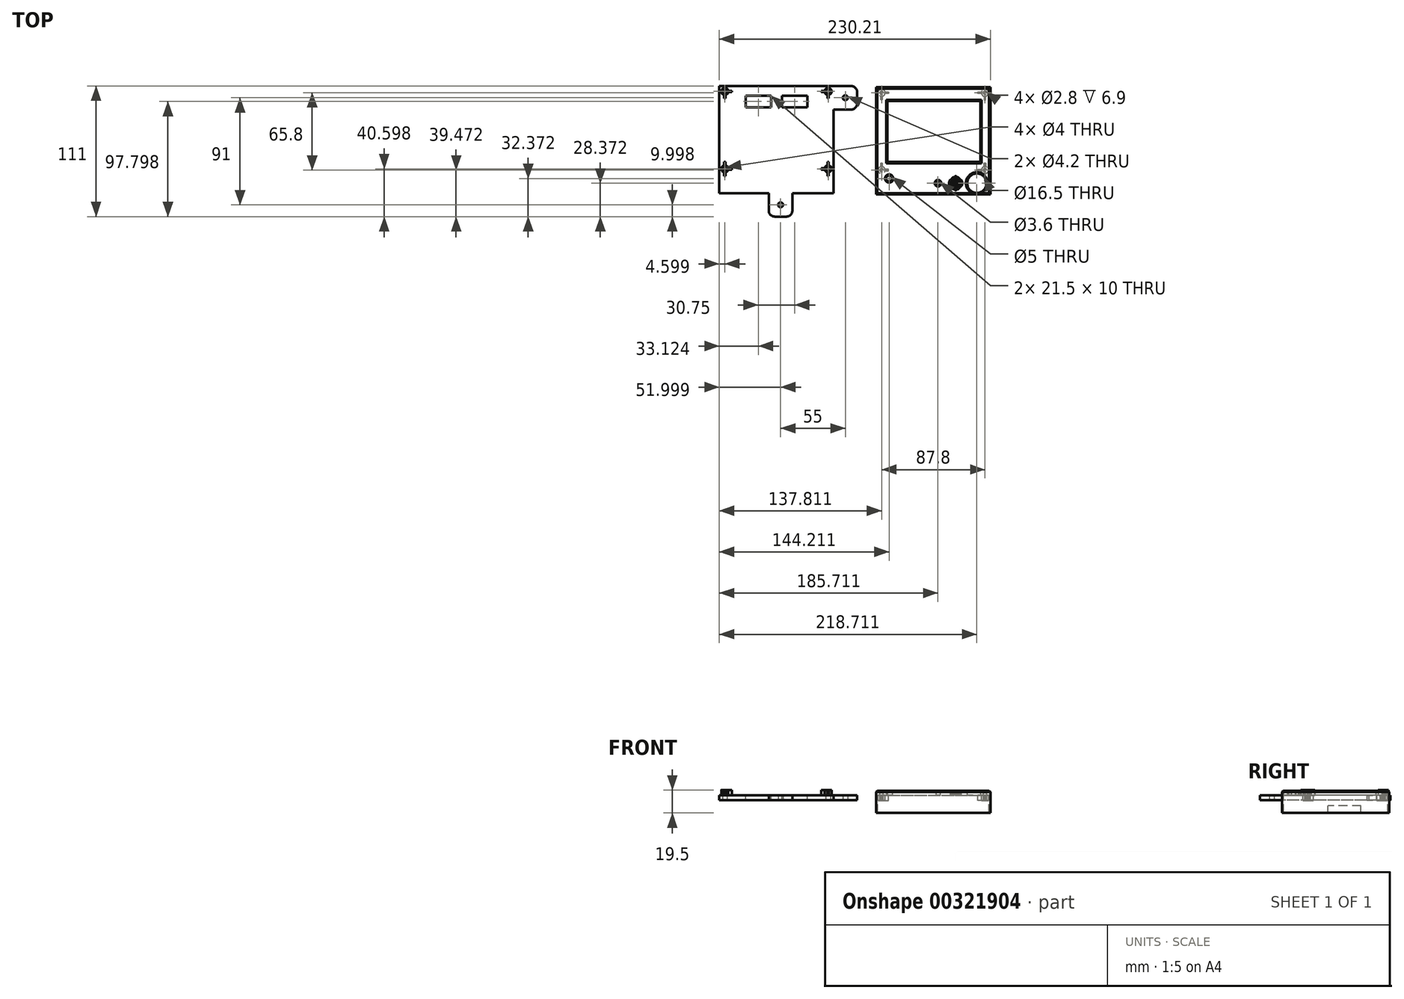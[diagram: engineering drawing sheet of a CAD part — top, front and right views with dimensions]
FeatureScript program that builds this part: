
annotation { "Feature Type Name" : "Feature", "Feature Type Description" : "" }
export const myFeature = defineFeature(function(context is Context, id is Id, definition is map)
    precondition{}
    {
        {
            var Q0;
            Q0=qCreatedBy(makeId("Top.planeOp"),FACE);
            var sketch = newSketch(context, id + "F0", { "sketchPlane" : qUnion([Q0])});
            skLineSegment(sketch, "E0.bottom", {"start": v(-33.99, 35.53) * mm, "end": v(63.01, 35.53) * mm});
            skLineSegment(sketch, "E0.top", {"start": v(-33.99, -55.47) * mm, "end": v(63.01, -55.47) * mm});
            skLineSegment(sketch, "E0.left", {"start": v(-33.99, 35.53) * mm, "end": v(-33.99, -55.47) * mm});
            skLineSegment(sketch, "E0.right", {"start": v(63.01, 35.53) * mm, "end": v(63.01, -55.47) * mm});
            skLineSegment(sketch, "E1.bottom", {"start": v(-24.49, 24.03) * mm, "end": v(54.51, 24.03) * mm});
            skLineSegment(sketch, "E1.top", {"start": v(-24.49, -27.97) * mm, "end": v(54.51, -27.97) * mm});
            skLineSegment(sketch, "E1.left", {"start": v(-24.49, 24.03) * mm, "end": v(-24.49, -27.97) * mm});
            skLineSegment(sketch, "E1.right", {"start": v(54.51, 24.03) * mm, "end": v(54.51, -27.97) * mm});
            skCircle(sketch, "E2", {"center": v(-29.39, 30.93) * mm, "radius": 1.4 * mm});
            skCircle(sketch, "E3", {"center": v(58.41, 30.93) * mm, "radius": 1.4 * mm});
            skCircle(sketch, "E4", {"center": v(58.41, -34.87) * mm, "radius": 1.4 * mm});
            skCircle(sketch, "E5", {"center": v(-29.39, -34.87) * mm, "radius": 1.4 * mm});
            skCircle(sketch, "E6", {"center": v(51.51, -45.97) * mm, "radius": 8.25 * mm});
            skEllipse(sketch, "E7", {"center": v(33.51, -45.97) * mm, "majorRadius": 5 * mm, "minorRadius": 0.55 * mm, "majorAxis": v(0, -1)});
            skEllipse(sketch, "E8", {"center": v(31.51, -45.97) * mm, "majorRadius": 4 * mm, "minorRadius": 0.55 * mm, "majorAxis": v(0, -1)});
            skEllipse(sketch, "E9", {"center": v(29.51, -45.97) * mm, "majorRadius": 2 * mm, "minorRadius": 0.55 * mm, "majorAxis": v(0, -1)});
            skEllipse(sketch, "E10", {"center": v(35.51, -45.97) * mm, "majorRadius": 4 * mm, "minorRadius": 0.55 * mm, "majorAxis": v(0, -1)});
            skPoint(sketch, "E10.centerSnap0", {"position": v(34.06, -45.97) * mm});
            skEllipse(sketch, "E11", {"center": v(37.51, -45.97) * mm, "majorRadius": 2 * mm, "minorRadius": 0.55 * mm, "majorAxis": v(0, -1)});
            skCircle(sketch, "E12", {"center": v(18.51, -45.97) * mm, "radius": 1.8 * mm});
            skPoint(sketch, "E12.centerSnap0", {"position": v(32.96, -45.97) * mm});
            skCircle(sketch, "E13", {"center": v(-22.99, -41.97) * mm, "radius": 2.5 * mm});
            skSolve(sketch);
        }
        {
            var Q0;
            Q0=makeQuery(id+"F0.imprint","IMPRINT",FACE,{"disambiguationData":[TD([[makeQuery(id+"F0.imprint","IMPRINT",EDGE,{"derivedFrom":sQuery(id+"F0.wireOp",EDGE,"E0.bottom")}),-1.0]])]});
            var Q1;
            Q1=makeQuery(id+"F0.imprint","IMPRINT",FACE,{"disambiguationData":[TD([[makeQuery(id+"F0.imprint","IMPRINT",EDGE,{"derivedFrom":sQuery(id+"F0.wireOp",EDGE,"E2")}),1.0]])]});
            var Q2;
            Q2=makeQuery(id+"F0.imprint","IMPRINT",FACE,{"disambiguationData":[TD([[makeQuery(id+"F0.imprint","IMPRINT",EDGE,{"derivedFrom":sQuery(id+"F0.wireOp",EDGE,"E5")}),1.0]])]});
            var Q3;
            Q3=makeQuery(id+"F0.imprint","IMPRINT",FACE,{"disambiguationData":[TD([[makeQuery(id+"F0.imprint","IMPRINT",EDGE,{"derivedFrom":sQuery(id+"F0.wireOp",EDGE,"E4")}),1.0]])]});
            var Q4;
            Q4=makeQuery(id+"F0.imprint","IMPRINT",FACE,{"disambiguationData":[TD([[makeQuery(id+"F0.imprint","IMPRINT",EDGE,{"derivedFrom":sQuery(id+"F0.wireOp",EDGE,"E3")}),1.0]])]});
            extrude(context, id + "F1", {"entities" : qUnion([Q0, Q1, Q2, Q3, Q4]), "depth" : 4 * mm});
        }
        {
            var Q0;
            Q0=makeQuery(id+"F1.opExtrude","CAP_FACE",FACE,{"disambiguationData":[OSD([sQuery(id+"F0.wireOp",EDGE,"E0.bottom"),sQuery(id+"F0.wireOp",EDGE,"E0.top"),sQuery(id+"F0.wireOp",EDGE,"E0.left"),sQuery(id+"F0.wireOp",EDGE,"E0.right"),sQuery(id+"F0.wireOp",EDGE,"E1.bottom"),sQuery(id+"F0.wireOp",EDGE,"E1.top"),sQuery(id+"F0.wireOp",EDGE,"E1.left"),sQuery(id+"F0.wireOp",EDGE,"E1.right"),sQuery(id+"F0.wireOp",EDGE,"E2"),sQuery(id+"F0.wireOp",EDGE,"E3"),sQuery(id+"F0.wireOp",EDGE,"E4"),sQuery(id+"F0.wireOp",EDGE,"E5"),sQuery(id+"F0.wireOp",EDGE,"E6"),sQuery(id+"F0.wireOp",EDGE,"E7"),sQuery(id+"F0.wireOp",EDGE,"E8"),sQuery(id+"F0.wireOp",EDGE,"E9"),sQuery(id+"F0.wireOp",EDGE,"E10"),sQuery(id+"F0.wireOp",EDGE,"E11"),sQuery(id+"F0.wireOp",EDGE,"E12"),sQuery(id+"F0.wireOp",EDGE,"E13")])],"isStart":true});
            var sketch = newSketch(context, id + "F2", { "sketchPlane" : qUnion([Q0])});
            skCircle(sketch, "E14", {"center": v(58.41, -30.93) * mm, "radius": 1.4 * mm});
            skCircle(sketch, "E15", {"center": v(-29.39, -30.93) * mm, "radius": 1.4 * mm});
            skCircle(sketch, "E16", {"center": v(-29.39, 34.87) * mm, "radius": 1.4 * mm});
            skCircle(sketch, "E17", {"center": v(58.41, 34.87) * mm, "radius": 1.4 * mm});
            skLineSegment(sketch, "E18", {"start": v(61.81, -34.33) * mm, "end": v(-32.79, -34.33) * mm});
            skLineSegment(sketch, "E19", {"start": v(-32.79, -34.33) * mm, "end": v(-32.79, 54.27) * mm});
            skLineSegment(sketch, "E20", {"start": v(-32.79, 54.27) * mm, "end": v(61.81, 54.27) * mm});
            skLineSegment(sketch, "E21", {"start": v(61.81, 54.27) * mm, "end": v(61.81, -34.33) * mm});
            skCircle(sketch, "E22", {"center": v(58.41, -30.93) * mm, "radius": 3 * mm});
            skCircle(sketch, "E23", {"center": v(58.41, 34.87) * mm, "radius": 3 * mm});
            skCircle(sketch, "E24", {"center": v(-29.39, 34.87) * mm, "radius": 3 * mm});
            skCircle(sketch, "E25", {"center": v(-29.39, -30.93) * mm, "radius": 3 * mm});
            skLineSegment(sketch, "E26", {"start": v(55.47, 35.47) * mm, "end": v(52.41, 35.47) * mm});
            skLineSegment(sketch, "E27", {"start": v(52.41, 35.47) * mm, "end": v(52.41, 34.27) * mm});
            skLineSegment(sketch, "E28", {"start": v(52.41, 34.27) * mm, "end": v(55.47, 34.27) * mm});
            skLineSegment(sketch, "E29", {"start": v(57.81, 31.93) * mm, "end": v(57.81, 28.87) * mm});
            skLineSegment(sketch, "E30", {"start": v(57.81, 28.87) * mm, "end": v(59.01, 28.87) * mm});
            skLineSegment(sketch, "E31", {"start": v(59.01, 28.87) * mm, "end": v(59.01, 31.93) * mm});
            skLineSegment(sketch, "E32", {"start": v(57.81, -28) * mm, "end": v(57.81, -24.93) * mm});
            skLineSegment(sketch, "E33", {"start": v(57.81, -24.93) * mm, "end": v(59.01, -24.93) * mm});
            skLineSegment(sketch, "E34", {"start": v(59.01, -24.93) * mm, "end": v(59.01, -28) * mm});
            skLineSegment(sketch, "E35", {"start": v(55.47, -30.33) * mm, "end": v(52.41, -30.33) * mm});
            skLineSegment(sketch, "E36", {"start": v(52.41, -30.33) * mm, "end": v(52.41, -31.53) * mm});
            skLineSegment(sketch, "E37", {"start": v(52.41, -31.53) * mm, "end": v(55.47, -31.53) * mm});
            skLineSegment(sketch, "E38", {"start": v(-26.45, -31.53) * mm, "end": v(-23.39, -31.53) * mm});
            skLineSegment(sketch, "E39", {"start": v(-23.39, -31.53) * mm, "end": v(-23.39, -30.33) * mm});
            skLineSegment(sketch, "E40", {"start": v(-23.39, -30.33) * mm, "end": v(-26.45, -30.33) * mm});
            skLineSegment(sketch, "E41", {"start": v(-28.79, -28) * mm, "end": v(-28.79, -24.93) * mm});
            skLineSegment(sketch, "E42", {"start": v(-28.79, -24.93) * mm, "end": v(-29.99, -24.93) * mm});
            skLineSegment(sketch, "E43", {"start": v(-29.99, -24.93) * mm, "end": v(-29.99, -28) * mm});
            skLineSegment(sketch, "E44", {"start": v(-29.99, 31.93) * mm, "end": v(-29.99, 28.87) * mm});
            skLineSegment(sketch, "E45", {"start": v(-29.99, 28.87) * mm, "end": v(-28.79, 28.87) * mm});
            skLineSegment(sketch, "E46", {"start": v(-28.79, 28.87) * mm, "end": v(-28.79, 31.93) * mm});
            skLineSegment(sketch, "E47", {"start": v(-26.45, 35.47) * mm, "end": v(-23.39, 35.47) * mm});
            skLineSegment(sketch, "E48", {"start": v(-23.39, 35.47) * mm, "end": v(-23.39, 34.27) * mm});
            skLineSegment(sketch, "E49", {"start": v(-23.39, 34.27) * mm, "end": v(-26.45, 34.27) * mm});
            skSolve(sketch);
        }
        {
            var Q0;
            Q0=makeQuery(id+"F2.imprint","IMPRINT",FACE,{"disambiguationData":[TD([[makeQuery(id+"F2.imprint","IMPRINT",EDGE,{"derivedFrom":sQuery(id+"F2.wireOp",EDGE,"E18")}),1.0]])]});
            extrude(context, id + "F3", {"entities" : qUnion([Q0]), "operationType" : NewBodyOperationType.ADD, "depth" : 15 * mm});
        }
        {
            var Q0;
            Q0=makeQuery(id+"F2.imprint","IMPRINT",FACE,{"disambiguationData":[TD([[makeQuery(id+"F2.imprint","IMPRINT",EDGE,{"derivedFrom":sQuery(id+"F2.wireOp",EDGE,"E14")}),-1.0]])]});
            var Q1;
            Q1=makeQuery(id+"F2.imprint","IMPRINT",FACE,{"disambiguationData":[TD([[makeQuery(id+"F2.imprint","IMPRINT",EDGE,{"derivedFrom":sQuery(id+"F2.wireOp",EDGE,"E17")}),-1.0]])]});
            var Q2;
            Q2=makeQuery(id+"F2.imprint","IMPRINT",FACE,{"disambiguationData":[TD([[makeQuery(id+"F2.imprint","IMPRINT",EDGE,{"derivedFrom":sQuery(id+"F2.wireOp",EDGE,"E15")}),-1.0]])]});
            var Q3;
            Q3=makeQuery(id+"F2.imprint","IMPRINT",FACE,{"disambiguationData":[TD([[makeQuery(id+"F2.imprint","IMPRINT",EDGE,{"derivedFrom":sQuery(id+"F2.wireOp",EDGE,"E16")}),-1.0]])]});
            var Q4;
            {var subQ0=sQuery(id+"F2.wireOp",EDGE,"E44");Q4=makeQuery(id+"F2.imprint","IMPRINT",FACE,{"disambiguationData":[TD([[makeQuery(id+"F2.imprint","IMPRINT",EDGE,{"derivedFrom":subQ0}),1.0]])]});}
            var Q5;
            {var subQ0=sQuery(id+"F2.wireOp",EDGE,"E47");Q5=makeQuery(id+"F2.imprint","IMPRINT",FACE,{"disambiguationData":[TD([[makeQuery(id+"F2.imprint","IMPRINT",EDGE,{"derivedFrom":subQ0}),-1.0]])]});}
            var Q6;
            {var subQ0=sQuery(id+"F2.wireOp",EDGE,"E41");Q6=makeQuery(id+"F2.imprint","IMPRINT",FACE,{"disambiguationData":[TD([[makeQuery(id+"F2.imprint","IMPRINT",EDGE,{"derivedFrom":subQ0}),1.0]])]});}
            var Q7;
            {var subQ0=sQuery(id+"F2.wireOp",EDGE,"E38");Q7=makeQuery(id+"F2.imprint","IMPRINT",FACE,{"disambiguationData":[TD([[makeQuery(id+"F2.imprint","IMPRINT",EDGE,{"derivedFrom":subQ0}),1.0]])]});}
            var Q8;
            {var subQ0=sQuery(id+"F2.wireOp",EDGE,"E26");Q8=makeQuery(id+"F2.imprint","IMPRINT",FACE,{"disambiguationData":[TD([[makeQuery(id+"F2.imprint","IMPRINT",EDGE,{"derivedFrom":subQ0}),1.0]])]});}
            var Q9;
            {var subQ0=sQuery(id+"F2.wireOp",EDGE,"E29");Q9=makeQuery(id+"F2.imprint","IMPRINT",FACE,{"disambiguationData":[TD([[makeQuery(id+"F2.imprint","IMPRINT",EDGE,{"derivedFrom":subQ0}),1.0]])]});}
            var Q10;
            {var subQ0=sQuery(id+"F2.wireOp",EDGE,"E32");Q10=makeQuery(id+"F2.imprint","IMPRINT",FACE,{"disambiguationData":[TD([[makeQuery(id+"F2.imprint","IMPRINT",EDGE,{"derivedFrom":subQ0}),-1.0]])]});}
            var Q11;
            {var subQ0=sQuery(id+"F2.wireOp",EDGE,"E35");Q11=makeQuery(id+"F2.imprint","IMPRINT",FACE,{"disambiguationData":[TD([[makeQuery(id+"F2.imprint","IMPRINT",EDGE,{"derivedFrom":subQ0}),1.0]])]});}
            extrude(context, id + "F4", {"entities" : qUnion([Q0, Q1, Q2, Q3, Q4, Q5, Q6, Q7, Q8, Q9, Q10, Q11]), "operationType" : NewBodyOperationType.ADD, "depth" : 4.5 * mm});
        }
        {
            var Q0;
            Q0=makeQuery(id+"F4.boolean.opBoolean","SPLIT",FACE,{"disambiguationData":[TD([makeQuery(id+"F4.opExtrude","SWEPT_FACE",FACE,{"disambiguationData":[OSD([sQuery(id+"F2.wireOp",EDGE,"E15")])]})])],"derivedFrom":makeQuery(id+"F1.opExtrude","CAP_FACE",FACE,{"disambiguationData":[OSD([sQuery(id+"F0.wireOp",EDGE,"E0.bottom"),sQuery(id+"F0.wireOp",EDGE,"E0.top"),sQuery(id+"F0.wireOp",EDGE,"E0.left"),sQuery(id+"F0.wireOp",EDGE,"E0.right"),sQuery(id+"F0.wireOp",EDGE,"E1.bottom"),sQuery(id+"F0.wireOp",EDGE,"E1.top"),sQuery(id+"F0.wireOp",EDGE,"E1.left"),sQuery(id+"F0.wireOp",EDGE,"E1.right"),sQuery(id+"F0.wireOp",EDGE,"E6"),sQuery(id+"F0.wireOp",EDGE,"E7"),sQuery(id+"F0.wireOp",EDGE,"E8"),sQuery(id+"F0.wireOp",EDGE,"E9"),sQuery(id+"F0.wireOp",EDGE,"E10"),sQuery(id+"F0.wireOp",EDGE,"E11"),sQuery(id+"F0.wireOp",EDGE,"E12"),sQuery(id+"F0.wireOp",EDGE,"E13")])],"isStart":true})});
            var Q1;
            Q1=makeQuery(id+"F4.boolean.opBoolean","SPLIT",FACE,{"disambiguationData":[TD([makeQuery(id+"F4.opExtrude","SWEPT_FACE",FACE,{"disambiguationData":[OSD([sQuery(id+"F2.wireOp",EDGE,"E16")])]})])],"derivedFrom":makeQuery(id+"F1.opExtrude","CAP_FACE",FACE,{"disambiguationData":[OSD([sQuery(id+"F0.wireOp",EDGE,"E0.bottom"),sQuery(id+"F0.wireOp",EDGE,"E0.top"),sQuery(id+"F0.wireOp",EDGE,"E0.left"),sQuery(id+"F0.wireOp",EDGE,"E0.right"),sQuery(id+"F0.wireOp",EDGE,"E1.bottom"),sQuery(id+"F0.wireOp",EDGE,"E1.top"),sQuery(id+"F0.wireOp",EDGE,"E1.left"),sQuery(id+"F0.wireOp",EDGE,"E1.right"),sQuery(id+"F0.wireOp",EDGE,"E6"),sQuery(id+"F0.wireOp",EDGE,"E7"),sQuery(id+"F0.wireOp",EDGE,"E8"),sQuery(id+"F0.wireOp",EDGE,"E9"),sQuery(id+"F0.wireOp",EDGE,"E10"),sQuery(id+"F0.wireOp",EDGE,"E11"),sQuery(id+"F0.wireOp",EDGE,"E12"),sQuery(id+"F0.wireOp",EDGE,"E13")])],"isStart":true})});
            var Q2;
            Q2=makeQuery(id+"F4.boolean.opBoolean","SPLIT",FACE,{"disambiguationData":[TD([makeQuery(id+"F4.opExtrude","SWEPT_FACE",FACE,{"disambiguationData":[OSD([sQuery(id+"F2.wireOp",EDGE,"E17")])]})])],"derivedFrom":makeQuery(id+"F1.opExtrude","CAP_FACE",FACE,{"disambiguationData":[OSD([sQuery(id+"F0.wireOp",EDGE,"E0.bottom"),sQuery(id+"F0.wireOp",EDGE,"E0.top"),sQuery(id+"F0.wireOp",EDGE,"E0.left"),sQuery(id+"F0.wireOp",EDGE,"E0.right"),sQuery(id+"F0.wireOp",EDGE,"E1.bottom"),sQuery(id+"F0.wireOp",EDGE,"E1.top"),sQuery(id+"F0.wireOp",EDGE,"E1.left"),sQuery(id+"F0.wireOp",EDGE,"E1.right"),sQuery(id+"F0.wireOp",EDGE,"E6"),sQuery(id+"F0.wireOp",EDGE,"E7"),sQuery(id+"F0.wireOp",EDGE,"E8"),sQuery(id+"F0.wireOp",EDGE,"E9"),sQuery(id+"F0.wireOp",EDGE,"E10"),sQuery(id+"F0.wireOp",EDGE,"E11"),sQuery(id+"F0.wireOp",EDGE,"E12"),sQuery(id+"F0.wireOp",EDGE,"E13")])],"isStart":true})});
            var Q3;
            Q3=makeQuery(id+"F4.boolean.opBoolean","SPLIT",FACE,{"disambiguationData":[TD([makeQuery(id+"F4.opExtrude","SWEPT_FACE",FACE,{"disambiguationData":[OSD([sQuery(id+"F2.wireOp",EDGE,"E14")])]})])],"derivedFrom":makeQuery(id+"F1.opExtrude","CAP_FACE",FACE,{"disambiguationData":[OSD([sQuery(id+"F0.wireOp",EDGE,"E0.bottom"),sQuery(id+"F0.wireOp",EDGE,"E0.top"),sQuery(id+"F0.wireOp",EDGE,"E0.left"),sQuery(id+"F0.wireOp",EDGE,"E0.right"),sQuery(id+"F0.wireOp",EDGE,"E1.bottom"),sQuery(id+"F0.wireOp",EDGE,"E1.top"),sQuery(id+"F0.wireOp",EDGE,"E1.left"),sQuery(id+"F0.wireOp",EDGE,"E1.right"),sQuery(id+"F0.wireOp",EDGE,"E6"),sQuery(id+"F0.wireOp",EDGE,"E7"),sQuery(id+"F0.wireOp",EDGE,"E8"),sQuery(id+"F0.wireOp",EDGE,"E9"),sQuery(id+"F0.wireOp",EDGE,"E10"),sQuery(id+"F0.wireOp",EDGE,"E11"),sQuery(id+"F0.wireOp",EDGE,"E12"),sQuery(id+"F0.wireOp",EDGE,"E13")])],"isStart":true})});
            extrude(context, id + "F5", {"entities" : qUnion([Q0, Q1, Q2, Q3]), "operationType" : NewBodyOperationType.REMOVE, "oppositeDirection" : true, "depth" : 2.4 * mm});
        }
        {
            var Q0;
            {var subQ0=sQuery(id+"F0.wireOp",EDGE,"E0.left");Q0=makeQuery(id+"F3.boolean.opBoolean","MERGE",FACE,{"derivedFrom":[makeQuery(id+"F1.opExtrude","SWEPT_FACE",FACE,{"disambiguationData":[OSD([subQ0])]}),makeQuery(id+"F3.opExtrude","SWEPT_FACE",FACE,{"disambiguationData":[OSD([subQ0])]})]});}
            var sketch = newSketch(context, id + "F6", { "sketchPlane" : qUnion([Q0])});
            skLineSegment(sketch, "E50.bottom", {"start": v(-11.53, -15) * mm, "end": v(16.47, -15) * mm});
            skLineSegment(sketch, "E50.top", {"start": v(-11.53, -9) * mm, "end": v(16.47, -9) * mm});
            skLineSegment(sketch, "E50.left", {"start": v(-11.53, -15) * mm, "end": v(-11.53, -9) * mm});
            skLineSegment(sketch, "E50.right", {"start": v(16.47, -15) * mm, "end": v(16.47, -9) * mm});
            skSolve(sketch);
        }
        {
            var Q0;
            Q0=makeQuery(id+"F6.imprint","IMPRINT",FACE,{"disambiguationData":[TD([[makeQuery(id+"F6.imprint","IMPRINT",EDGE,{"derivedFrom":sQuery(id+"F6.wireOp",EDGE,"E50.bottom")}),1.0]])]});
            extrude(context, id + "F7", {"entities" : qUnion([Q0]), "operationType" : NewBodyOperationType.REMOVE, "oppositeDirection" : true, "depth" : 2 * mm});
        }
        {
            var Q0;
            Q0=makeQuery(id+"F1.opExtrude","CAP_FACE",FACE,{"disambiguationData":[OSD([sQuery(id+"F0.wireOp",EDGE,"E0.bottom"),sQuery(id+"F0.wireOp",EDGE,"E0.top"),sQuery(id+"F0.wireOp",EDGE,"E0.left"),sQuery(id+"F0.wireOp",EDGE,"E0.right"),sQuery(id+"F0.wireOp",EDGE,"E1.bottom"),sQuery(id+"F0.wireOp",EDGE,"E1.top"),sQuery(id+"F0.wireOp",EDGE,"E1.left"),sQuery(id+"F0.wireOp",EDGE,"E1.right"),sQuery(id+"F0.wireOp",EDGE,"E6"),sQuery(id+"F0.wireOp",EDGE,"E7"),sQuery(id+"F0.wireOp",EDGE,"E8"),sQuery(id+"F0.wireOp",EDGE,"E9"),sQuery(id+"F0.wireOp",EDGE,"E10"),sQuery(id+"F0.wireOp",EDGE,"E11"),sQuery(id+"F0.wireOp",EDGE,"E12"),sQuery(id+"F0.wireOp",EDGE,"E13")])],"isStart":false});
            chamfer(context, id + "F8", {"entities" : qUnion([Q0]), "width" : 1 * mm, "tangentPropagation" : true});
        }
        {
            var Q0;
            Q0=qCreatedBy(makeId("Top.planeOp"),FACE);
            var sketch = newSketch(context, id + "F9", { "sketchPlane" : qUnion([Q0])});
            skLineSegment(sketch, "E51.bottom", {"start": v(-167.2, 36.66) * mm, "end": v(-70.2, 36.66) * mm});
            skLineSegment(sketch, "E51.top", {"start": v(-167.2, -54.34) * mm, "end": v(-70.2, -54.34) * mm});
            skLineSegment(sketch, "E51.left", {"start": v(-167.2, 36.66) * mm, "end": v(-167.2, -54.34) * mm});
            skLineSegment(sketch, "E51.right", {"start": v(-70.2, 36.66) * mm, "end": v(-70.2, -54.34) * mm});
            skLineSegment(sketch, "E52.bottom", {"start": v(-166, 35.46) * mm, "end": v(-71.4, 35.46) * mm});
            skLineSegment(sketch, "E52.top", {"start": v(-166, -53.14) * mm, "end": v(-71.4, -53.14) * mm});
            skLineSegment(sketch, "E52.left", {"start": v(-166, 35.46) * mm, "end": v(-166, -53.14) * mm});
            skLineSegment(sketch, "E52.right", {"start": v(-71.4, 35.46) * mm, "end": v(-71.4, -53.14) * mm});
            skCircle(sketch, "E53", {"center": v(-162.6, 32.06) * mm, "radius": 2 * mm});
            skCircle(sketch, "E54", {"center": v(-74.8, 32.06) * mm, "radius": 2 * mm});
            skCircle(sketch, "E55", {"center": v(-162.6, -33.74) * mm, "radius": 2 * mm});
            skCircle(sketch, "E56", {"center": v(-74.8, -33.74) * mm, "radius": 2 * mm});
            skLineSegment(sketch, "E57", {"start": v(-71.4, -33.74) * mm, "end": v(-71.4, -33.74) * mm});
            skLineSegment(sketch, "E58.bottom", {"start": v(-144.83, 28.46) * mm, "end": v(-123.33, 28.46) * mm});
            skLineSegment(sketch, "E58.top", {"start": v(-144.83, 18.46) * mm, "end": v(-123.33, 18.46) * mm});
            skLineSegment(sketch, "E58.left", {"start": v(-144.83, 28.46) * mm, "end": v(-144.83, 18.46) * mm});
            skLineSegment(sketch, "E58.right", {"start": v(-123.33, 28.46) * mm, "end": v(-123.33, 18.46) * mm});
            skLineSegment(sketch, "E59.bottom", {"start": v(-114.08, 28.46) * mm, "end": v(-92.58, 28.46) * mm});
            skLineSegment(sketch, "E59.top", {"start": v(-114.08, 18.46) * mm, "end": v(-92.58, 18.46) * mm});
            skLineSegment(sketch, "E59.left", {"start": v(-114.08, 28.46) * mm, "end": v(-114.08, 18.46) * mm});
            skLineSegment(sketch, "E59.right", {"start": v(-92.58, 28.46) * mm, "end": v(-92.58, 18.46) * mm});
            skCircle(sketch, "E60", {"center": v(-74.8, 32.06) * mm, "radius": 3 * mm});
            skCircle(sketch, "E61", {"center": v(-162.6, 32.06) * mm, "radius": 3 * mm});
            skCircle(sketch, "E62", {"center": v(-74.8, -33.74) * mm, "radius": 3 * mm});
            skCircle(sketch, "E63", {"center": v(-162.6, -33.74) * mm, "radius": 3 * mm});
            skLineSegment(sketch, "E64", {"start": v(-163.2, 29.12) * mm, "end": v(-163.2, 26.06) * mm});
            skLineSegment(sketch, "E65", {"start": v(-163.2, 26.06) * mm, "end": v(-162, 26.06) * mm});
            skLineSegment(sketch, "E66", {"start": v(-162, 26.06) * mm, "end": v(-162, 29.12) * mm});
            skLineSegment(sketch, "E67", {"start": v(-159.66, 32.66) * mm, "end": v(-156.6, 32.66) * mm});
            skLineSegment(sketch, "E68", {"start": v(-156.6, 32.66) * mm, "end": v(-156.6, 31.46) * mm});
            skLineSegment(sketch, "E69", {"start": v(-156.6, 31.46) * mm, "end": v(-159.66, 31.46) * mm});
            skLineSegment(sketch, "E70", {"start": v(-163.2, -30.8) * mm, "end": v(-163.2, -27.74) * mm});
            skLineSegment(sketch, "E71", {"start": v(-163.2, -27.74) * mm, "end": v(-162, -27.74) * mm});
            skLineSegment(sketch, "E72", {"start": v(-162, -27.74) * mm, "end": v(-162, -30.8) * mm});
            skLineSegment(sketch, "E73", {"start": v(-159.66, -33.14) * mm, "end": v(-156.6, -33.14) * mm});
            skLineSegment(sketch, "E74", {"start": v(-156.6, -33.14) * mm, "end": v(-156.6, -34.34) * mm});
            skLineSegment(sketch, "E75", {"start": v(-156.6, -34.34) * mm, "end": v(-159.66, -34.34) * mm});
            skLineSegment(sketch, "E76", {"start": v(-162, -36.68) * mm, "end": v(-162, -39.74) * mm});
            skLineSegment(sketch, "E77", {"start": v(-162, -39.74) * mm, "end": v(-163.2, -39.74) * mm});
            skLineSegment(sketch, "E78", {"start": v(-163.2, -39.74) * mm, "end": v(-163.2, -36.68) * mm});
            skLineSegment(sketch, "E79", {"start": v(-75.4, -30.8) * mm, "end": v(-75.4, -27.74) * mm});
            skLineSegment(sketch, "E80", {"start": v(-75.4, -27.74) * mm, "end": v(-74.2, -27.74) * mm});
            skLineSegment(sketch, "E81", {"start": v(-74.2, -27.74) * mm, "end": v(-74.2, -30.8) * mm});
            skLineSegment(sketch, "E82", {"start": v(-77.74, -33.14) * mm, "end": v(-80.8, -33.14) * mm});
            skLineSegment(sketch, "E83", {"start": v(-80.8, -33.14) * mm, "end": v(-80.8, -34.34) * mm});
            skLineSegment(sketch, "E84", {"start": v(-80.8, -34.34) * mm, "end": v(-77.74, -34.34) * mm});
            skLineSegment(sketch, "E85", {"start": v(-75.4, -36.68) * mm, "end": v(-75.4, -39.74) * mm});
            skLineSegment(sketch, "E86", {"start": v(-75.4, -39.74) * mm, "end": v(-74.2, -39.74) * mm});
            skLineSegment(sketch, "E87", {"start": v(-74.2, -39.74) * mm, "end": v(-74.2, -36.68) * mm});
            skLineSegment(sketch, "E88", {"start": v(-77.74, 32.66) * mm, "end": v(-80.8, 32.66) * mm});
            skLineSegment(sketch, "E89", {"start": v(-80.8, 32.66) * mm, "end": v(-80.8, 31.46) * mm});
            skLineSegment(sketch, "E90", {"start": v(-80.8, 31.46) * mm, "end": v(-77.74, 31.46) * mm});
            skLineSegment(sketch, "E91", {"start": v(-75.4, 29.12) * mm, "end": v(-75.4, 26.06) * mm});
            skLineSegment(sketch, "E92", {"start": v(-75.4, 26.06) * mm, "end": v(-74.2, 26.06) * mm});
            skLineSegment(sketch, "E93", {"start": v(-74.2, 26.06) * mm, "end": v(-74.2, 29.12) * mm});
            skSolve(sketch);
        }
        {
            var Q0;
            Q0=makeQuery(id+"F9.imprint","IMPRINT",FACE,{"disambiguationData":[TD([[makeQuery(id+"F9.imprint","IMPRINT",EDGE,{"derivedFrom":sQuery(id+"F9.wireOp",EDGE,"E53")}),-1.0]])]});
            var Q1;
            Q1=makeQuery(id+"F9.imprint","IMPRINT",FACE,{"disambiguationData":[TD([[makeQuery(id+"F9.imprint","IMPRINT",EDGE,{"derivedFrom":sQuery(id+"F9.wireOp",EDGE,"E54")}),-1.0]])]});
            var Q2;
            Q2=makeQuery(id+"F9.imprint","IMPRINT",FACE,{"disambiguationData":[TD([[makeQuery(id+"F9.imprint","IMPRINT",EDGE,{"derivedFrom":sQuery(id+"F9.wireOp",EDGE,"E56")}),-1.0]])]});
            var Q3;
            Q3=makeQuery(id+"F9.imprint","IMPRINT",FACE,{"disambiguationData":[TD([[makeQuery(id+"F9.imprint","IMPRINT",EDGE,{"derivedFrom":sQuery(id+"F9.wireOp",EDGE,"E55")}),-1.0]])]});
            var Q4;
            {var subQ0=sQuery(id+"F9.wireOp",EDGE,"E64");Q4=makeQuery(id+"F9.imprint","IMPRINT",FACE,{"disambiguationData":[TD([[makeQuery(id+"F9.imprint","IMPRINT",EDGE,{"derivedFrom":subQ0}),1.0]])]});}
            var Q5;
            {var subQ0=sQuery(id+"F9.wireOp",EDGE,"E67");Q5=makeQuery(id+"F9.imprint","IMPRINT",FACE,{"disambiguationData":[TD([[makeQuery(id+"F9.imprint","IMPRINT",EDGE,{"derivedFrom":subQ0}),-1.0]])]});}
            var Q6;
            {var subQ0=sQuery(id+"F9.wireOp",EDGE,"E76");Q6=makeQuery(id+"F9.imprint","IMPRINT",FACE,{"disambiguationData":[TD([[makeQuery(id+"F9.imprint","IMPRINT",EDGE,{"derivedFrom":subQ0}),-1.0]])]});}
            var Q7;
            {var subQ0=sQuery(id+"F9.wireOp",EDGE,"E70");Q7=makeQuery(id+"F9.imprint","IMPRINT",FACE,{"disambiguationData":[TD([[makeQuery(id+"F9.imprint","IMPRINT",EDGE,{"derivedFrom":subQ0}),-1.0]])]});}
            var Q8;
            {var subQ0=sQuery(id+"F9.wireOp",EDGE,"E73");Q8=makeQuery(id+"F9.imprint","IMPRINT",FACE,{"disambiguationData":[TD([[makeQuery(id+"F9.imprint","IMPRINT",EDGE,{"derivedFrom":subQ0}),-1.0]])]});}
            var Q9;
            {var subQ0=sQuery(id+"F9.wireOp",EDGE,"E85");Q9=makeQuery(id+"F9.imprint","IMPRINT",FACE,{"disambiguationData":[TD([[makeQuery(id+"F9.imprint","IMPRINT",EDGE,{"derivedFrom":subQ0}),1.0]])]});}
            var Q10;
            {var subQ0=sQuery(id+"F9.wireOp",EDGE,"E82");Q10=makeQuery(id+"F9.imprint","IMPRINT",FACE,{"disambiguationData":[TD([[makeQuery(id+"F9.imprint","IMPRINT",EDGE,{"derivedFrom":subQ0}),1.0]])]});}
            var Q11;
            {var subQ0=sQuery(id+"F9.wireOp",EDGE,"E79");Q11=makeQuery(id+"F9.imprint","IMPRINT",FACE,{"disambiguationData":[TD([[makeQuery(id+"F9.imprint","IMPRINT",EDGE,{"derivedFrom":subQ0}),-1.0]])]});}
            var Q12;
            {var subQ0=sQuery(id+"F9.wireOp",EDGE,"E91");Q12=makeQuery(id+"F9.imprint","IMPRINT",FACE,{"disambiguationData":[TD([[makeQuery(id+"F9.imprint","IMPRINT",EDGE,{"derivedFrom":subQ0}),1.0]])]});}
            var Q13;
            {var subQ0=sQuery(id+"F9.wireOp",EDGE,"E88");Q13=makeQuery(id+"F9.imprint","IMPRINT",FACE,{"disambiguationData":[TD([[makeQuery(id+"F9.imprint","IMPRINT",EDGE,{"derivedFrom":subQ0}),1.0]])]});}
            extrude(context, id + "F10", {"entities" : qUnion([Q0, Q1, Q2, Q3, Q4, Q5, Q6, Q7, Q8, Q9, Q10, Q11, Q12, Q13]), "depth" : 4.5 * mm});
        }
        {
            var Q0;
            Q0=makeQuery(id+"F9.imprint","IMPRINT",FACE,{"disambiguationData":[TD([[makeQuery(id+"F9.imprint","IMPRINT",EDGE,{"derivedFrom":sQuery(id+"F9.wireOp",EDGE,"E51.bottom")}),-1.0]])]});
            var Q1;
            Q1=makeQuery(id+"F9.imprint","IMPRINT",FACE,{"disambiguationData":[TD([[makeQuery(id+"F9.imprint","IMPRINT",EDGE,{"derivedFrom":sQuery(id+"F9.wireOp",EDGE,"E53")}),-1.0]])]});
            var Q2;
            Q2=makeQuery(id+"F9.imprint","IMPRINT",FACE,{"disambiguationData":[TD([[makeQuery(id+"F9.imprint","IMPRINT",EDGE,{"derivedFrom":sQuery(id+"F9.wireOp",EDGE,"E55")}),-1.0]])]});
            var Q3;
            Q3=makeQuery(id+"F9.imprint","IMPRINT",FACE,{"disambiguationData":[TD([[makeQuery(id+"F9.imprint","IMPRINT",EDGE,{"derivedFrom":sQuery(id+"F9.wireOp",EDGE,"E56")}),-1.0]])]});
            var Q4;
            Q4=makeQuery(id+"F9.imprint","IMPRINT",FACE,{"disambiguationData":[TD([[makeQuery(id+"F9.imprint","IMPRINT",EDGE,{"derivedFrom":sQuery(id+"F9.wireOp",EDGE,"E54")}),-1.0]])]});
            var Q5;
            {var subQ0=sQuery(id+"F9.wireOp",EDGE,"E88");Q5=makeQuery(id+"F9.imprint","IMPRINT",FACE,{"disambiguationData":[TD([[makeQuery(id+"F9.imprint","IMPRINT",EDGE,{"derivedFrom":subQ0}),1.0]])]});}
            var Q6;
            {var subQ0=sQuery(id+"F9.wireOp",EDGE,"E91");Q6=makeQuery(id+"F9.imprint","IMPRINT",FACE,{"disambiguationData":[TD([[makeQuery(id+"F9.imprint","IMPRINT",EDGE,{"derivedFrom":subQ0}),1.0]])]});}
            var Q7;
            {var subQ0=sQuery(id+"F9.wireOp",EDGE,"E64");Q7=makeQuery(id+"F9.imprint","IMPRINT",FACE,{"disambiguationData":[TD([[makeQuery(id+"F9.imprint","IMPRINT",EDGE,{"derivedFrom":subQ0}),1.0]])]});}
            var Q8;
            {var subQ0=sQuery(id+"F9.wireOp",EDGE,"E67");Q8=makeQuery(id+"F9.imprint","IMPRINT",FACE,{"disambiguationData":[TD([[makeQuery(id+"F9.imprint","IMPRINT",EDGE,{"derivedFrom":subQ0}),-1.0]])]});}
            var Q9;
            {var subQ0=sQuery(id+"F9.wireOp",EDGE,"E73");Q9=makeQuery(id+"F9.imprint","IMPRINT",FACE,{"disambiguationData":[TD([[makeQuery(id+"F9.imprint","IMPRINT",EDGE,{"derivedFrom":subQ0}),-1.0]])]});}
            var Q10;
            {var subQ0=sQuery(id+"F9.wireOp",EDGE,"E70");Q10=makeQuery(id+"F9.imprint","IMPRINT",FACE,{"disambiguationData":[TD([[makeQuery(id+"F9.imprint","IMPRINT",EDGE,{"derivedFrom":subQ0}),-1.0]])]});}
            var Q11;
            Q11=makeQuery(id+"F9.imprint","IMPRINT",FACE,{"disambiguationData":[TD([[makeQuery(id+"F9.imprint","IMPRINT",EDGE,{"derivedFrom":sQuery(id+"F9.wireOp",EDGE,"E52.bottom")}),-1.0]])]});
            var Q12;
            {var subQ0=sQuery(id+"F9.wireOp",EDGE,"E76");Q12=makeQuery(id+"F9.imprint","IMPRINT",FACE,{"disambiguationData":[TD([[makeQuery(id+"F9.imprint","IMPRINT",EDGE,{"derivedFrom":subQ0}),-1.0]])]});}
            var Q13;
            {var subQ0=sQuery(id+"F9.wireOp",EDGE,"E85");Q13=makeQuery(id+"F9.imprint","IMPRINT",FACE,{"disambiguationData":[TD([[makeQuery(id+"F9.imprint","IMPRINT",EDGE,{"derivedFrom":subQ0}),1.0]])]});}
            var Q14;
            {var subQ0=sQuery(id+"F9.wireOp",EDGE,"E82");Q14=makeQuery(id+"F9.imprint","IMPRINT",FACE,{"disambiguationData":[TD([[makeQuery(id+"F9.imprint","IMPRINT",EDGE,{"derivedFrom":subQ0}),1.0]])]});}
            var Q15;
            {var subQ0=sQuery(id+"F9.wireOp",EDGE,"E79");Q15=makeQuery(id+"F9.imprint","IMPRINT",FACE,{"disambiguationData":[TD([[makeQuery(id+"F9.imprint","IMPRINT",EDGE,{"derivedFrom":subQ0}),-1.0]])]});}
            extrude(context, id + "F11", {"entities" : qUnion([Q0, Q1, Q2, Q3, Q4, Q5, Q6, Q7, Q8, Q9, Q10, Q11, Q12, Q13, Q14, Q15]), "operationType" : NewBodyOperationType.ADD, "oppositeDirection" : true, "depth" : 4 * mm});
        }
        {
            var Q0;
            Q0=makeQuery(id+"F11.opExtrude","SWEPT_FACE",FACE,{"disambiguationData":[OSD([sQuery(id+"F9.wireOp",EDGE,"E51.right")])]});
            var sketch = newSketch(context, id + "F12", { "sketchPlane" : qUnion([Q0])});
            skLineSegment(sketch, "E94", {"start": v(16.66, 0) * mm, "end": v(16.66, -4) * mm});
            skSolve(sketch);
        }
        {
            var Q0;
            {var subQ0=sQuery(id+"F12.wireOp",EDGE,"E94");Q0=makeQuery(id+"F12.imprint","IMPRINT",FACE,{"disambiguationData":[TD([[makeQuery(id+"F12.imprint","IMPRINT",EDGE,{"derivedFrom":subQ0}),1.0]])]});}
            extrude(context, id + "F13", {"entities" : qUnion([Q0]), "operationType" : NewBodyOperationType.ADD, "depth" : 20 * mm});
        }
        {
            var Q0;
            Q0=makeQuery(id+"F11.opExtrude","SWEPT_FACE",FACE,{"disambiguationData":[OSD([sQuery(id+"F9.wireOp",EDGE,"E51.top")])]});
            var sketch = newSketch(context, id + "F14", { "sketchPlane" : qUnion([Q0])});
            skLineSegment(sketch, "E95", {"start": v(-105.2, -4) * mm, "end": v(-105.2, 0) * mm});
            skLineSegment(sketch, "E96", {"start": v(-125.2, -4) * mm, "end": v(-125.2, 0) * mm});
            skSolve(sketch);
        }
        {
            var Q0;
            {var subQ0=sQuery(id+"F14.wireOp",EDGE,"E95");Q0=makeQuery(id+"F14.imprint","IMPRINT",FACE,{"disambiguationData":[TD([[makeQuery(id+"F14.imprint","IMPRINT",EDGE,{"derivedFrom":subQ0}),1.0]])]});}
            extrude(context, id + "F15", {"entities" : qUnion([Q0]), "operationType" : NewBodyOperationType.ADD, "depth" : 20 * mm});
        }
        {
            var Q0;
            {var subQ0=sQuery(id+"F9.wireOp",EDGE,"E51.top");var subQ1=makeQuery(id+"F11.opExtrude","CAP_EDGE",EDGE,{"disambiguationData":[OSD([subQ0])],"isStart":false});var subQ2=sQuery(id+"F9.wireOp",EDGE,"E51.right");var subQ3=makeQuery(id+"F11.opExtrude","CAP_EDGE",EDGE,{"disambiguationData":[OSD([subQ2])],"isStart":false});var subQ4=sQuery(id+"F9.wireOp",EDGE,"E51.bottom");Q0=makeQuery(id+"F15.boolean.opBoolean","MERGE",FACE,{"derivedFrom":[makeQuery(id+"F13.boolean.opBoolean","MERGE",FACE,{"derivedFrom":[makeQuery(id+"F11.opExtrude","CAP_FACE",FACE,{"disambiguationData":[OSD([subQ4,subQ0,sQuery(id+"F9.wireOp",EDGE,"E51.left"),subQ2,sQuery(id+"F9.wireOp",EDGE,"E53"),sQuery(id+"F9.wireOp",EDGE,"E54"),sQuery(id+"F9.wireOp",EDGE,"E55"),sQuery(id+"F9.wireOp",EDGE,"E56"),sQuery(id+"F9.wireOp",EDGE,"E58.bottom"),sQuery(id+"F9.wireOp",EDGE,"E58.top"),sQuery(id+"F9.wireOp",EDGE,"E58.left"),sQuery(id+"F9.wireOp",EDGE,"E58.right"),sQuery(id+"F9.wireOp",EDGE,"E59.bottom"),sQuery(id+"F9.wireOp",EDGE,"E59.top"),sQuery(id+"F9.wireOp",EDGE,"E59.left"),sQuery(id+"F9.wireOp",EDGE,"E59.right")])],"isStart":false}),makeQuery(id+"F13.opExtrude","SWEPT_FACE",FACE,{"disambiguationData":[OSD([subQ2]),TDD([makeQuery(id+"F12.imprint","IMPRINT",EDGE,{"disambiguationData":[TD([[makeQuery(id+"F12.imprint","INTERSECT",VERTEX,{"derivedFrom":[subQ3,sQuery(id+"F12.wireOp",EDGE,"E94")]}),1.0]])],"derivedFrom":subQ3})])]})]}),makeQuery(id+"F15.opExtrude","SWEPT_FACE",FACE,{"disambiguationData":[OSD([subQ0]),TDD([makeQuery(id+"F14.imprint","IMPRINT",EDGE,{"disambiguationData":[TD([[makeQuery(id+"F14.imprint","INTERSECT",VERTEX,{"derivedFrom":[subQ1,sQuery(id+"F14.wireOp",EDGE,"E95")]}),1.0]])],"derivedFrom":subQ1})])]})]});}
            var sketch = newSketch(context, id + "F16", { "sketchPlane" : qUnion([Q0])});
            skCircle(sketch, "E97", {"center": v(-60.2, -26.66) * mm, "radius": 2.1 * mm});
            skPoint(sketch, "E97.centerSnap0", {"position": v(-60.2, -16.66) * mm});
            skPoint(sketch, "E97.centerSnap1", {"position": v(-50.2, -26.66) * mm});
            skCircle(sketch, "E98", {"center": v(-115.2, 64.34) * mm, "radius": 2.1 * mm});
            skPoint(sketch, "E98.centerSnap0", {"position": v(-115.2, 74.34) * mm});
            skPoint(sketch, "E98.centerSnap1", {"position": v(-125.2, 64.34) * mm});
            skSolve(sketch);
        }
        {
            var Q0;
            Q0=makeQuery(id+"F16.imprint","IMPRINT",FACE,{"disambiguationData":[TD([[makeQuery(id+"F16.imprint","IMPRINT",EDGE,{"derivedFrom":sQuery(id+"F16.wireOp",EDGE,"E97")}),1.0]])]});
            var Q1;
            Q1=makeQuery(id+"F16.imprint","IMPRINT",FACE,{"disambiguationData":[TD([[makeQuery(id+"F16.imprint","IMPRINT",EDGE,{"derivedFrom":sQuery(id+"F16.wireOp",EDGE,"E98")}),1.0]])]});
            extrude(context, id + "F17", {"entities" : qUnion([Q0, Q1]), "operationType" : NewBodyOperationType.REMOVE, "endBound" : BoundingType.THROUGH_ALL, "oppositeDirection" : true, "depth" : 25 * mm});
        }
        {
            var Q0;
            Q0=makeQuery(id+"F13.opExtrude","CAP_EDGE",EDGE,{"disambiguationData":[OSD([sQuery(id+"F9.wireOp",EDGE,"E51.bottom"),sQuery(id+"F9.wireOp",EDGE,"E51.right")])],"isStart":false});
            var Q1;
            Q1=makeQuery(id+"F13.opExtrude","CAP_EDGE",EDGE,{"disambiguationData":[OSD([sQuery(id+"F12.wireOp",EDGE,"E94")])],"isStart":false});
            var Q2;
            Q2=makeQuery(id+"F15.opExtrude","CAP_EDGE",EDGE,{"disambiguationData":[OSD([sQuery(id+"F14.wireOp",EDGE,"E95")])],"isStart":false});
            var Q3;
            Q3=makeQuery(id+"F15.opExtrude","CAP_EDGE",EDGE,{"disambiguationData":[OSD([sQuery(id+"F14.wireOp",EDGE,"E96")])],"isStart":false});
            fillet(context, id + "F18", {"entities" : qUnion([Q0, Q1, Q2, Q3]), "radius" : 5 * mm, "tangentPropagation" : true, "allowEdgeOverflow" : false});
        }
    });
